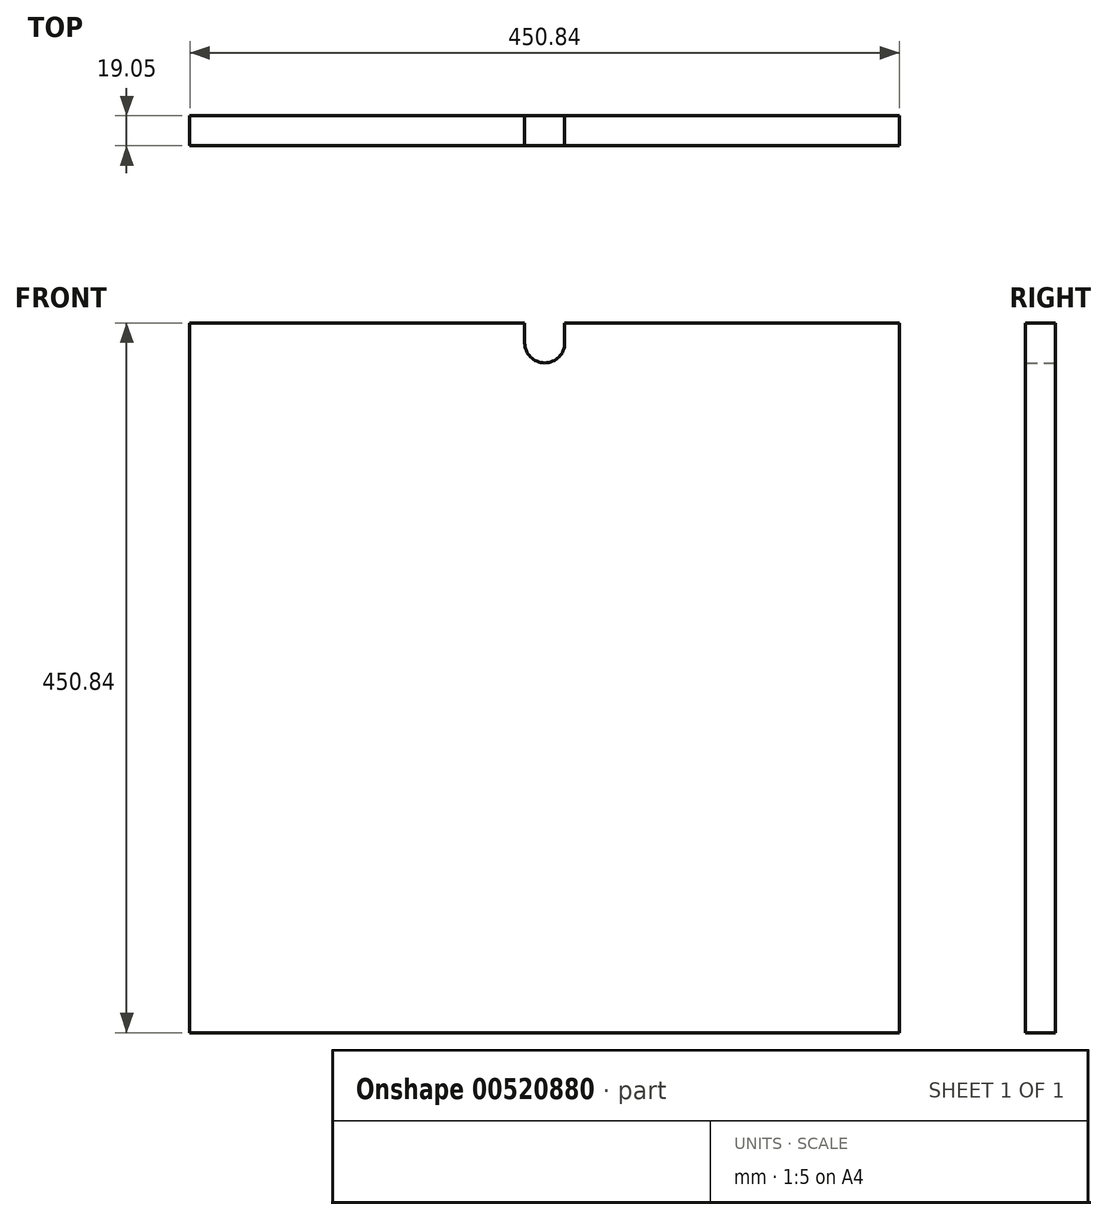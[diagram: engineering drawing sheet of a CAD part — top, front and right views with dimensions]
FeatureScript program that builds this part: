
annotation { "Feature Type Name" : "Feature", "Feature Type Description" : "" }
export const myFeature = defineFeature(function(context is Context, id is Id, definition is map)
    precondition{}
    {
        {
            var Q0;
            Q0=qCreatedBy(makeId("Front.planeOp"),FACE);
            var sketch = newSketch(context, id + "F0", { "sketchPlane" : qUnion([Q0])});
            skLineSegment(sketch, "E0.bottom", {"start": v(225.43, 225.43) * mm, "end": v(-225.42, 225.43) * mm});
            skLineSegment(sketch, "E0.top", {"start": v(225.42, -225.42) * mm, "end": v(-225.43, -225.42) * mm});
            skLineSegment(sketch, "E0.left", {"start": v(225.43, 225.43) * mm, "end": v(225.42, -225.42) * mm});
            skLineSegment(sketch, "E0.right", {"start": v(-225.43, 225.43) * mm, "end": v(-225.43, -225.42) * mm});
            skPoint(sketch, "E0.middle", {"position": v(0, 0) * mm});
            skLineSegment(sketch, "E1.bottom", {"start": v(12.7, 212.73) * mm, "end": v(-12.7, 212.73) * mm});
            skLineSegment(sketch, "E1.top", {"start": v(12.7, 238.13) * mm, "end": v(-12.7, 238.13) * mm});
            skLineSegment(sketch, "E1.left", {"start": v(12.7, 212.73) * mm, "end": v(12.7, 238.13) * mm});
            skLineSegment(sketch, "E1.right", {"start": v(-12.7, 212.73) * mm, "end": v(-12.7, 238.13) * mm});
            skPoint(sketch, "E1.middle", {"position": v(0, 225.43) * mm});
            skCircle(sketch, "E2", {"center": v(0, 212.73) * mm, "radius": 12.7 * mm});
            skSolve(sketch);
        }
        {
            var Q0;
            Q0=makeQuery(id+"F0.imprint","IMPRINT",FACE,{"disambiguationData":[TD([[makeQuery(id+"F0.imprint","IMPRINT",EDGE,{"derivedFrom":sQuery(id+"F0.wireOp",EDGE,"E0.top")}),-1.0]])]});
            extrude(context, id + "F1", {"entities" : qUnion([Q0]), "depth" : 19.05 * mm, "offsetDistance" : 25.4 * mm});
        }
    });
